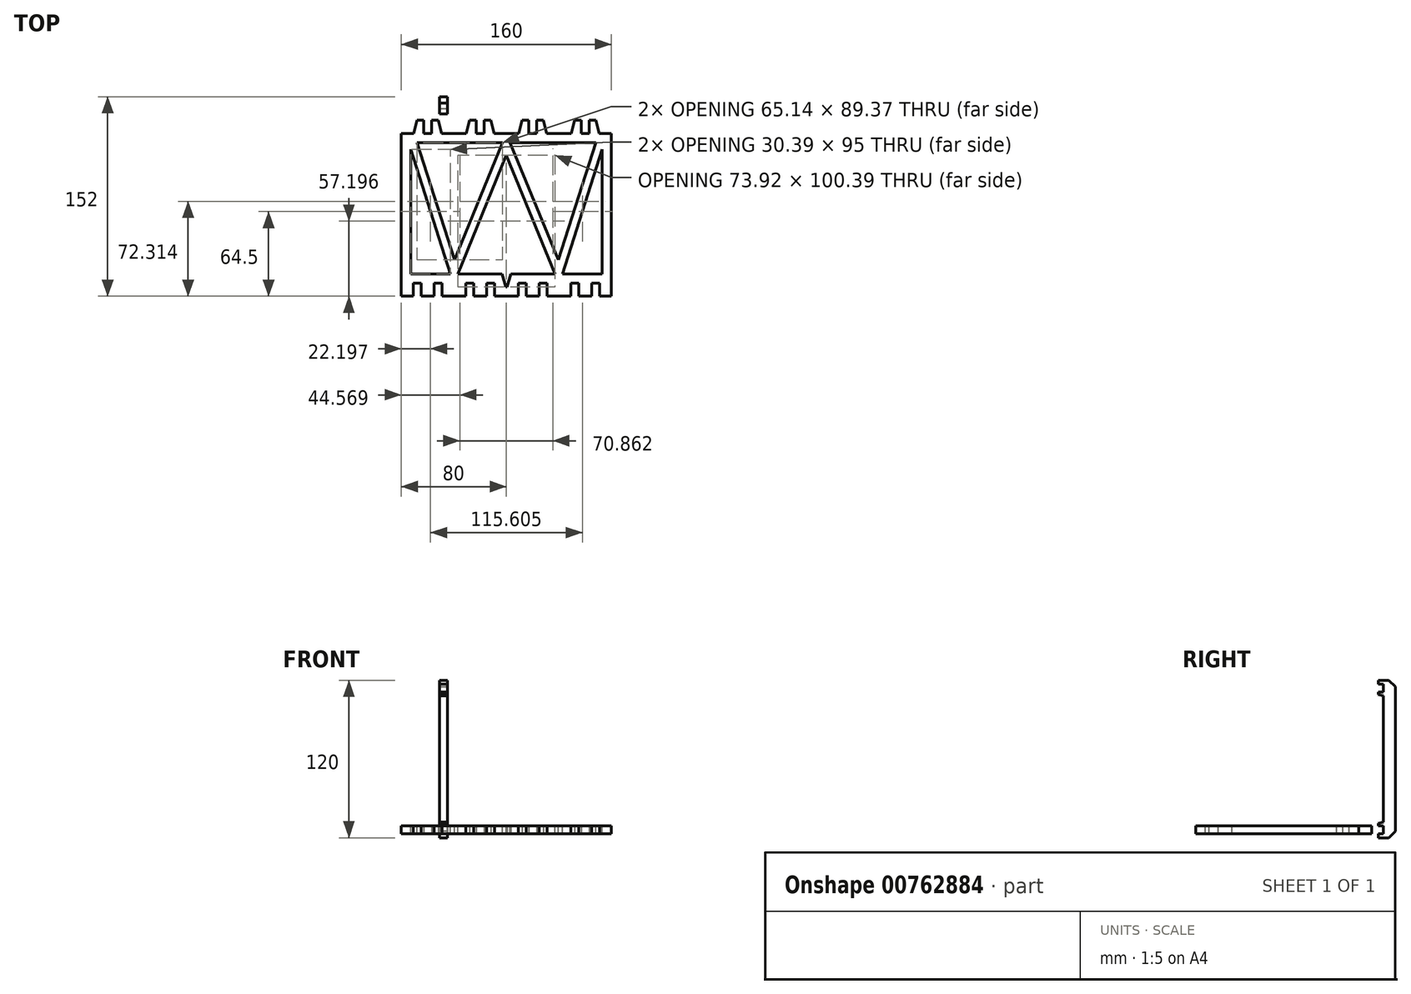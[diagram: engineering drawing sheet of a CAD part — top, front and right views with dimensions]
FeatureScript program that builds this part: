
annotation { "Feature Type Name" : "Feature", "Feature Type Description" : "" }
export const myFeature = defineFeature(function(context is Context, id is Id, definition is map)
    precondition{}
    {
        {
            assignVariable(context, id + "F0", {"name" : "bar_thick", "anyValue" : 6});
        }
        {
            var Q0;
            Q0=qCreatedBy(makeId("Top.planeOp"),FACE);
            var sketch = newSketch(context, id + "F1", { "sketchPlane" : qUnion([Q0])});
            skLineSegment(sketch, "E0", {"start": v(-20, 0) * mm, "end": v(-10.62, 0) * mm});
            skLineSegment(sketch, "E1", {"start": v(-10.62, 0) * mm, "end": v(-8, 10) * mm});
            skLineSegment(sketch, "E2", {"start": v(-8, 10) * mm, "end": v(-3, 10) * mm});
            skLineSegment(sketch, "E3", {"start": v(-3, 10) * mm, "end": v(-3, 0) * mm});
            skLineSegment(sketch, "E4", {"start": v(0, 0) * mm, "end": v(0, -7) * mm, "construction": true});
            skLineSegment(sketch, "E5", {"start": v(-3, 0) * mm, "end": v(-10.62, 0) * mm, "construction": true});
            skLineSegment(sketch, "E6", {"start": v(-20, -117) * mm, "end": v(-19.4, -117) * mm});
            skLineSegment(sketch, "E7", {"start": v(-19.4, -117) * mm, "end": v(-16.79, -107) * mm});
            skLineSegment(sketch, "E8", {"start": v(-16.79, -107) * mm, "end": v(0, -107) * mm});
            skLineSegment(sketch, "E9", {"start": v(-20, -124) * mm, "end": v(-11, -124) * mm});
            skLineSegment(sketch, "E10", {"start": v(-11, -124) * mm, "end": v(-11, -114) * mm});
            skLineSegment(sketch, "E11", {"start": v(-11, -114) * mm, "end": v(-5, -114) * mm});
            skLineSegment(sketch, "E12", {"start": v(-5, -114) * mm, "end": v(-5, -124) * mm});
            skLineSegment(sketch, "E13", {"start": v(-5, -124) * mm, "end": v(0, -124) * mm});
            skLineSegment(sketch, "E14", {"start": v(0, -117) * mm, "end": v(0, -124) * mm, "construction": true});
            skLineSegment(sketch, "E15", {"start": v(0, -7) * mm, "end": v(0, -117) * mm, "construction": true});
            skLineSegment(sketch, "E16", {"start": v(-11, -114) * mm, "end": v(-18.62, -114) * mm, "construction": true});
            skLineSegment(sketch, "E17", {"start": v(-11, -114) * mm, "end": v(-11, -107) * mm, "construction": true});
            skLineSegment(sketch, "E18", {"start": v(-19.4, -117) * mm, "end": v(-19.4, -124) * mm, "construction": true});
            skLineSegment(sketch, "E19", {"start": v(0, -7) * mm, "end": v(-20, -7) * mm});
            skLineSegment(sketch, "E20", {"start": v(-3, 0) * mm, "end": v(0, 0) * mm});
            skLineSegment(sketch, "E21", {"start": v(-20, 0) * mm, "end": v(-20, -7) * mm});
            skLineSegment(sketch, "E22", {"start": v(-20, -117) * mm, "end": v(-20, -124) * mm});
            skLineSegment(sketch, "E23", {"start": v(0, 0) * mm, "end": v(0, -7) * mm});
            skLineSegment(sketch, "E24", {"start": v(0, -107) * mm, "end": v(0, -124) * mm});
            skSolve(sketch);
        }
        {
            var Q0;
            Q0=makeQuery(id+"F1.imprint","IMPRINT",FACE,{"disambiguationData":[TD([[makeQuery(id+"F1.imprint","IMPRINT",EDGE,{"derivedFrom":sQuery(id+"F1.wireOp",EDGE,"E0")}),-1.0]])]});
            var Q1;
            Q1=makeQuery(id+"F1.imprint","IMPRINT",FACE,{"disambiguationData":[TD([[makeQuery(id+"F1.imprint","IMPRINT",EDGE,{"derivedFrom":sQuery(id+"F1.wireOp",EDGE,"E6")}),-1.0]])]});
            extrude(context, id + "F2", {"entities" : qUnion([Q0, Q1]), "depth" : (getVariable(context, 'bar_thick')) * mm, "offsetDistance" : 25 * mm});
        }
        {
            var Q0;
            Q0=makeQuery(id+"F2.opExtrude","SWEPT_BODY",BODY,{"disambiguationData":[OSD([sQuery(id+"F1.wireOp",EDGE,"E0"),sQuery(id+"F1.wireOp",EDGE,"E1"),sQuery(id+"F1.wireOp",EDGE,"E2"),sQuery(id+"F1.wireOp",EDGE,"E3"),sQuery(id+"F1.wireOp",EDGE,"E19"),sQuery(id+"F1.wireOp",EDGE,"E20"),sQuery(id+"F1.wireOp",EDGE,"E21"),sQuery(id+"F1.wireOp",EDGE,"E23")])]});
            var Q1;
            Q1=makeQuery(id+"F2.opExtrude","SWEPT_BODY",BODY,{"disambiguationData":[OSD([sQuery(id+"F1.wireOp",EDGE,"E6"),sQuery(id+"F1.wireOp",EDGE,"E7"),sQuery(id+"F1.wireOp",EDGE,"E8"),sQuery(id+"F1.wireOp",EDGE,"E9"),sQuery(id+"F1.wireOp",EDGE,"E10"),sQuery(id+"F1.wireOp",EDGE,"E11"),sQuery(id+"F1.wireOp",EDGE,"E12"),sQuery(id+"F1.wireOp",EDGE,"E13"),sQuery(id+"F1.wireOp",EDGE,"E22"),sQuery(id+"F1.wireOp",EDGE,"E24")])]});
            var Q2;
            Q2=makeQuery(id+"F2.opExtrude","SWEPT_FACE",FACE,{"disambiguationData":[OSD([sQuery(id+"F1.wireOp",EDGE,"E23")])]});
            mirror(context, id + "F3", {"operationType" : NewBodyOperationType.ADD, "entities" : qUnion([Q0, Q1]), "mirrorPlane" : qUnion([Q2])});
        }
        {
            var Q0;
            Q0=makeQuery(id+"F2.opExtrude","SWEPT_BODY",BODY,{"disambiguationData":[OSD([sQuery(id+"F1.wireOp",EDGE,"E0"),sQuery(id+"F1.wireOp",EDGE,"E1"),sQuery(id+"F1.wireOp",EDGE,"E2"),sQuery(id+"F1.wireOp",EDGE,"E3"),sQuery(id+"F1.wireOp",EDGE,"E19"),sQuery(id+"F1.wireOp",EDGE,"E20"),sQuery(id+"F1.wireOp",EDGE,"E21"),sQuery(id+"F1.wireOp",EDGE,"E23")])]});
            var Q1;
            Q1=makeQuery(id+"F2.opExtrude","SWEPT_BODY",BODY,{"disambiguationData":[OSD([sQuery(id+"F1.wireOp",EDGE,"E6"),sQuery(id+"F1.wireOp",EDGE,"E7"),sQuery(id+"F1.wireOp",EDGE,"E8"),sQuery(id+"F1.wireOp",EDGE,"E9"),sQuery(id+"F1.wireOp",EDGE,"E10"),sQuery(id+"F1.wireOp",EDGE,"E11"),sQuery(id+"F1.wireOp",EDGE,"E12"),sQuery(id+"F1.wireOp",EDGE,"E13"),sQuery(id+"F1.wireOp",EDGE,"E22"),sQuery(id+"F1.wireOp",EDGE,"E24")])]});
            var Q2;
            Q2=makeQuery(id+"F3.opPattern","COPY",FACE,{"derivedFrom":makeQuery(id+"F2.opExtrude","SWEPT_FACE",FACE,{"disambiguationData":[OSD([sQuery(id+"F1.wireOp",EDGE,"E21")])]}),"instanceName":"1"});
            mirror(context, id + "F4", {"operationType" : NewBodyOperationType.ADD, "entities" : qUnion([Q0, Q1]), "mirrorPlane" : qUnion([Q2])});
        }
        {
            var Q0;
            Q0=makeQuery(id+"F2.opExtrude","SWEPT_BODY",BODY,{"disambiguationData":[OSD([sQuery(id+"F1.wireOp",EDGE,"E0"),sQuery(id+"F1.wireOp",EDGE,"E1"),sQuery(id+"F1.wireOp",EDGE,"E2"),sQuery(id+"F1.wireOp",EDGE,"E3"),sQuery(id+"F1.wireOp",EDGE,"E19"),sQuery(id+"F1.wireOp",EDGE,"E20"),sQuery(id+"F1.wireOp",EDGE,"E21"),sQuery(id+"F1.wireOp",EDGE,"E23")])]});
            var Q1;
            Q1=makeQuery(id+"F2.opExtrude","SWEPT_BODY",BODY,{"disambiguationData":[OSD([sQuery(id+"F1.wireOp",EDGE,"E6"),sQuery(id+"F1.wireOp",EDGE,"E7"),sQuery(id+"F1.wireOp",EDGE,"E8"),sQuery(id+"F1.wireOp",EDGE,"E9"),sQuery(id+"F1.wireOp",EDGE,"E10"),sQuery(id+"F1.wireOp",EDGE,"E11"),sQuery(id+"F1.wireOp",EDGE,"E12"),sQuery(id+"F1.wireOp",EDGE,"E13"),sQuery(id+"F1.wireOp",EDGE,"E22"),sQuery(id+"F1.wireOp",EDGE,"E24")])]});
            var Q2;
            Q2=makeQuery(id+"F4.opPattern","COPY",FACE,{"derivedFrom":makeQuery(id+"F2.opExtrude","SWEPT_FACE",FACE,{"disambiguationData":[OSD([sQuery(id+"F1.wireOp",EDGE,"E21")])]}),"instanceName":"1"});
            mirror(context, id + "F5", {"operationType" : NewBodyOperationType.ADD, "entities" : qUnion([Q0, Q1]), "mirrorPlane" : qUnion([Q2])});
        }
        {
            var Q0;
            {var subQ0=makeQuery(id+"F2.opExtrude","CAP_FACE",FACE,{"disambiguationData":[OSD([sQuery(id+"F1.wireOp",EDGE,"E0"),sQuery(id+"F1.wireOp",EDGE,"E1"),sQuery(id+"F1.wireOp",EDGE,"E2"),sQuery(id+"F1.wireOp",EDGE,"E3"),sQuery(id+"F1.wireOp",EDGE,"E19"),sQuery(id+"F1.wireOp",EDGE,"E20"),sQuery(id+"F1.wireOp",EDGE,"E21"),sQuery(id+"F1.wireOp",EDGE,"E23")])],"isStart":false});var subQ1=makeQuery(id+"F3.boolean.opBoolean","MERGE",FACE,{"derivedFrom":[subQ0,makeQuery(id+"F3.opPattern","COPY",FACE,{"derivedFrom":subQ0,"instanceName":"1"})]});var subQ2=makeQuery(id+"F4.boolean.opBoolean","MERGE",FACE,{"derivedFrom":[subQ1,makeQuery(id+"F4.opPattern","COPY",FACE,{"derivedFrom":subQ1,"instanceName":"1"})]});Q0=makeQuery(id+"F5.boolean.opBoolean","MERGE",FACE,{"derivedFrom":[subQ2,makeQuery(id+"F5.opPattern","COPY",FACE,{"derivedFrom":subQ2,"instanceName":"1"})]});}
            var sketch = newSketch(context, id + "F6", { "sketchPlane" : qUnion([Q0])});
            skLineSegment(sketch, "E25", {"start": v(-20, -7) * mm, "end": v(-20, -117) * mm});
            skLineSegment(sketch, "E26", {"start": v(-20, -7) * mm, "end": v(-13, -7) * mm});
            skLineSegment(sketch, "E27", {"start": v(-13, -7) * mm, "end": v(-13, -117) * mm});
            skLineSegment(sketch, "E28", {"start": v(-13, -117) * mm, "end": v(-20, -117) * mm});
            skLineSegment(sketch, "E29", {"start": v(-20, -7) * mm, "end": v(-20, 0) * mm, "construction": true});
            skLineSegment(sketch, "E30", {"start": v(60, -7) * mm, "end": v(60, -117) * mm, "construction": true});
            skLineSegment(sketch, "E31.MirrorCS", {"start": v(140, -7) * mm, "end": v(133, -7) * mm});
            skLineSegment(sketch, "E32.MirrorCS", {"start": v(133, -117) * mm, "end": v(140, -117) * mm});
            skLineSegment(sketch, "E33.MirrorCS", {"start": v(140, -7) * mm, "end": v(140, -117) * mm});
            skLineSegment(sketch, "E34.MirrorCS", {"start": v(133, -7) * mm, "end": v(133, -117) * mm});
            skSolve(sketch);
        }
        {
            var Q0;
            Q0 = qSketchRegion(id + "F6", true);
            var Q1;
            {var subQ0=makeQuery(id+"F2.opExtrude","CAP_FACE",FACE,{"disambiguationData":[OSD([sQuery(id+"F1.wireOp",EDGE,"E0"),sQuery(id+"F1.wireOp",EDGE,"E1"),sQuery(id+"F1.wireOp",EDGE,"E2"),sQuery(id+"F1.wireOp",EDGE,"E3"),sQuery(id+"F1.wireOp",EDGE,"E19"),sQuery(id+"F1.wireOp",EDGE,"E20"),sQuery(id+"F1.wireOp",EDGE,"E21"),sQuery(id+"F1.wireOp",EDGE,"E23")])],"isStart":true});var subQ1=makeQuery(id+"F3.boolean.opBoolean","MERGE",FACE,{"derivedFrom":[subQ0,makeQuery(id+"F3.opPattern","COPY",FACE,{"derivedFrom":subQ0,"instanceName":"1"})]});var subQ2=makeQuery(id+"F4.boolean.opBoolean","MERGE",FACE,{"derivedFrom":[subQ1,makeQuery(id+"F4.opPattern","COPY",FACE,{"derivedFrom":subQ1,"instanceName":"1"})]});Q1=makeQuery(id+"F5.boolean.opBoolean","MERGE",FACE,{"derivedFrom":[subQ2,makeQuery(id+"F5.opPattern","COPY",FACE,{"derivedFrom":subQ2,"instanceName":"1"})]});}
            extrude(context, id + "F7", {"entities" : qUnion([Q0]), "operationType" : NewBodyOperationType.ADD, "endBound" : BoundingType.UP_TO_SURFACE, "oppositeDirection" : true, "depth" : 25 * mm, "endBoundEntityFace" : qUnion([Q1]), "offsetDistance" : 25 * mm});
        }
        {
            var Q0;
            {var subQ0=makeQuery(id+"F2.opExtrude","CAP_FACE",FACE,{"disambiguationData":[OSD([sQuery(id+"F1.wireOp",EDGE,"E6"),sQuery(id+"F1.wireOp",EDGE,"E7"),sQuery(id+"F1.wireOp",EDGE,"E8"),sQuery(id+"F1.wireOp",EDGE,"E9"),sQuery(id+"F1.wireOp",EDGE,"E10"),sQuery(id+"F1.wireOp",EDGE,"E11"),sQuery(id+"F1.wireOp",EDGE,"E12"),sQuery(id+"F1.wireOp",EDGE,"E13"),sQuery(id+"F1.wireOp",EDGE,"E22"),sQuery(id+"F1.wireOp",EDGE,"E24")])],"isStart":false});var subQ1=makeQuery(id+"F3.boolean.opBoolean","MERGE",FACE,{"derivedFrom":[subQ0,makeQuery(id+"F3.opPattern","COPY",FACE,{"derivedFrom":subQ0,"instanceName":"1"})]});var subQ2=makeQuery(id+"F4.boolean.opBoolean","MERGE",FACE,{"derivedFrom":[subQ1,makeQuery(id+"F4.opPattern","COPY",FACE,{"derivedFrom":subQ1,"instanceName":"1"})]});var subQ3=makeQuery(id+"F2.opExtrude","CAP_FACE",FACE,{"disambiguationData":[OSD([sQuery(id+"F1.wireOp",EDGE,"E0"),sQuery(id+"F1.wireOp",EDGE,"E1"),sQuery(id+"F1.wireOp",EDGE,"E2"),sQuery(id+"F1.wireOp",EDGE,"E3"),sQuery(id+"F1.wireOp",EDGE,"E19"),sQuery(id+"F1.wireOp",EDGE,"E20"),sQuery(id+"F1.wireOp",EDGE,"E21"),sQuery(id+"F1.wireOp",EDGE,"E23")])],"isStart":false});var subQ4=makeQuery(id+"F3.boolean.opBoolean","MERGE",FACE,{"derivedFrom":[subQ3,makeQuery(id+"F3.opPattern","COPY",FACE,{"derivedFrom":subQ3,"instanceName":"1"})]});var subQ5=makeQuery(id+"F4.boolean.opBoolean","MERGE",FACE,{"derivedFrom":[subQ4,makeQuery(id+"F4.opPattern","COPY",FACE,{"derivedFrom":subQ4,"instanceName":"1"})]});Q0=makeQuery(id+"F7.boolean.opBoolean","MERGE",FACE,{"derivedFrom":[makeQuery(id+"F5.boolean.opBoolean","MERGE",FACE,{"derivedFrom":[subQ5,makeQuery(id+"F5.opPattern","COPY",FACE,{"derivedFrom":subQ5,"instanceName":"1"})]}),makeQuery(id+"F5.boolean.opBoolean","MERGE",FACE,{"derivedFrom":[subQ2,makeQuery(id+"F5.opPattern","COPY",FACE,{"derivedFrom":subQ2,"instanceName":"1"})]}),makeQuery(id+"F7.opExtrude","CAP_FACE",FACE,{"disambiguationData":[OSD([sQuery(id+"F6.wireOp",EDGE,"E25"),sQuery(id+"F6.wireOp",EDGE,"E26"),sQuery(id+"F6.wireOp",EDGE,"E27"),sQuery(id+"F6.wireOp",EDGE,"E28")])],"isStart":true}),makeQuery(id+"F7.opExtrude","CAP_FACE",FACE,{"disambiguationData":[OSD([sQuery(id+"F6.wireOp",EDGE,"E31.MirrorCS"),sQuery(id+"F6.wireOp",EDGE,"E32.MirrorCS"),sQuery(id+"F6.wireOp",EDGE,"E33.MirrorCS"),sQuery(id+"F6.wireOp",EDGE,"E34.MirrorCS")])],"isStart":true})]});}
            var sketch = newSketch(context, id + "F8", { "sketchPlane" : qUnion([Q0])});
            skLineSegment(sketch, "E35", {"start": v(-13, -7) * mm, "end": v(-8, -7) * mm});
            skLineSegment(sketch, "E36", {"start": v(-8, -7) * mm, "end": v(20.6, -96.37) * mm});
            skLineSegment(sketch, "E37", {"start": v(20.6, -96.37) * mm, "end": v(60, 0) * mm});
            skLineSegment(sketch, "E38", {"start": v(60, 0) * mm, "end": v(60, -16.6) * mm});
            skLineSegment(sketch, "E39", {"start": v(60, -16.6) * mm, "end": v(23.04, -107) * mm});
            skLineSegment(sketch, "E40", {"start": v(-13, -7) * mm, "end": v(-13, -12) * mm});
            skLineSegment(sketch, "E41", {"start": v(20.6, -117) * mm, "end": v(23.21, -107) * mm});
            skLineSegment(sketch, "E42", {"start": v(23.04, -107) * mm, "end": v(23.21, -107) * mm});
            skLineSegment(sketch, "E43", {"start": v(20.6, -117) * mm, "end": v(-13, -12) * mm});
            skLineSegment(sketch, "E44", {"start": v(40.3, -48.19) * mm, "end": v(46.12, -50.57) * mm, "construction": true});
            skLineSegment(sketch, "E45", {"start": v(6.3, -51.69) * mm, "end": v(0.31, -53.6) * mm, "construction": true});
            skLineSegment(sketch, "E46.MirrorCS", {"start": v(99.4, -96.37) * mm, "end": v(60, 0) * mm});
            skLineSegment(sketch, "E47.MirrorCS", {"start": v(60, -16.6) * mm, "end": v(96.96, -107) * mm});
            skLineSegment(sketch, "E48.MirrorCS", {"start": v(96.96, -107) * mm, "end": v(96.79, -107) * mm});
            skLineSegment(sketch, "E49.MirrorCS", {"start": v(99.4, -117) * mm, "end": v(96.79, -107) * mm});
            skLineSegment(sketch, "E50.MirrorCS", {"start": v(99.4, -117) * mm, "end": v(133, -12) * mm});
            skLineSegment(sketch, "E51.MirrorCS", {"start": v(128, -7) * mm, "end": v(99.4, -96.37) * mm});
            skLineSegment(sketch, "E52.MirrorCS", {"start": v(133, -7) * mm, "end": v(128, -7) * mm});
            skLineSegment(sketch, "E53.MirrorCS", {"start": v(133, -7) * mm, "end": v(133, -12) * mm});
            skLineSegment(sketch, "E54", {"start": v(16.79, -107) * mm, "end": v(17.4, -107) * mm});
            skLineSegment(sketch, "E55", {"start": v(16.79, -107) * mm, "end": v(19.4, -117) * mm});
            skLineSegment(sketch, "E56", {"start": v(19.4, -117) * mm, "end": v(20.6, -117) * mm});
            skLineSegment(sketch, "E57.MirrorCS", {"start": v(100.6, -117) * mm, "end": v(99.4, -117) * mm});
            skLineSegment(sketch, "E58.MirrorCS", {"start": v(103.21, -107) * mm, "end": v(100.6, -117) * mm});
            skLineSegment(sketch, "E59.MirrorCS", {"start": v(103.21, -107) * mm, "end": v(102.6, -107) * mm});
            skSolve(sketch);
        }
        {
            var Q0;
            Q0=makeQuery(id+"F8.imprint","IMPRINT",FACE,{"disambiguationData":[TD([[makeQuery(id+"F8.imprint","IMPRINT",EDGE,{"derivedFrom":sQuery(id+"F8.wireOp",EDGE,"E35")}),1.0]])]});
            var Q1;
            {var subQ0=sQuery(id+"F8.wireOp",EDGE,"E47.MirrorCS");Q1=makeQuery(id+"F8.imprint","IMPRINT",FACE,{"disambiguationData":[TD([[makeQuery(id+"F8.imprint","IMPRINT",EDGE,{"derivedFrom":subQ0}),1.0]])]});}
            var Q2;
            {var subQ2=sQuery(id+"F8.wireOp",EDGE,"E54");Q2=makeQuery(id+"F8.imprint","IMPRINT",FACE,{"disambiguationData":[TD([[makeQuery(id+"F8.imprint","IMPRINT",EDGE,{"derivedFrom":subQ2}),-1.0]])]});}
            var Q3;
            {var subQ0=sQuery(id+"F8.wireOp",EDGE,"E57.MirrorCS");Q3=makeQuery(id+"F8.imprint","IMPRINT",FACE,{"disambiguationData":[TD([[makeQuery(id+"F8.imprint","IMPRINT",EDGE,{"derivedFrom":subQ0}),1.0]])]});}
            var Q4;
            Q4=makeQuery(id+"F7.opExtrude","CAP_VERTEX",VERTEX,{"disambiguationData":[OSD([sQuery(id+"F1.wireOp",EDGE,"E0"),sQuery(id+"F1.wireOp",EDGE,"E1"),sQuery(id+"F1.wireOp",EDGE,"E2"),sQuery(id+"F1.wireOp",EDGE,"E3"),sQuery(id+"F1.wireOp",EDGE,"E19"),sQuery(id+"F1.wireOp",EDGE,"E20"),sQuery(id+"F1.wireOp",EDGE,"E21"),sQuery(id+"F1.wireOp",EDGE,"E23"),sQuery(id+"F6.wireOp",EDGE,"E31.MirrorCS"),sQuery(id+"F6.wireOp",EDGE,"E34.MirrorCS")])],"isStart":false});
            extrude(context, id + "F9", {"entities" : qUnion([Q0, Q1, Q2, Q3]), "operationType" : NewBodyOperationType.ADD, "endBound" : BoundingType.UP_TO_VERTEX, "oppositeDirection" : true, "depth" : 25 * mm, "endBoundEntityVertex" : qUnion([Q4]), "offsetDistance" : 25 * mm});
        }
        {
            var Q0;
            Q0=qCreatedBy(makeId("Top.planeOp"),FACE);
            var sketch = newSketch(context, id + "F10", { "sketchPlane" : qUnion([Q0])});
            skLineSegment(sketch, "E60", {"start": v(0, 28) * mm, "end": v(0, 15) * mm});
            skLineSegment(sketch, "E61", {"start": v(0, 15) * mm, "end": v(3, 15) * mm});
            skLineSegment(sketch, "E62", {"start": v(3, 15) * mm, "end": v(3, 19) * mm});
            skLineSegment(sketch, "E63", {"start": v(3, 19) * mm, "end": v(9, 19) * mm});
            skLineSegment(sketch, "E64", {"start": v(9, 19) * mm, "end": v(9, 15) * mm});
            skLineSegment(sketch, "E65", {"start": v(0, 28) * mm, "end": v(60, 28) * mm});
            skLineSegment(sketch, "E66", {"start": v(60, 28) * mm, "end": v(60, 19) * mm, "construction": true});
            skLineSegment(sketch, "E67", {"start": v(9, 19) * mm, "end": v(9, 28) * mm, "construction": true});
            skLineSegment(sketch, "E68", {"start": v(9, 15) * mm, "end": v(11, 15) * mm});
            skLineSegment(sketch, "E69", {"start": v(11, 15) * mm, "end": v(12, 19) * mm});
            skLineSegment(sketch, "E70", {"start": v(12, 19) * mm, "end": v(60, 19) * mm});
            skLineSegment(sketch, "E71", {"start": v(9, 19) * mm, "end": v(12, 19) * mm, "construction": true});
            skLineSegment(sketch, "E72.MirrorCS", {"start": v(120, 15) * mm, "end": v(117, 15) * mm});
            skLineSegment(sketch, "E73.MirrorCS", {"start": v(111, 15) * mm, "end": v(109, 15) * mm});
            skLineSegment(sketch, "E74.MirrorCS", {"start": v(109, 15) * mm, "end": v(108, 19) * mm});
            skLineSegment(sketch, "E75.MirrorCS", {"start": v(111, 19) * mm, "end": v(111, 15) * mm});
            skLineSegment(sketch, "E76.MirrorCS", {"start": v(117, 15) * mm, "end": v(117, 19) * mm});
            skLineSegment(sketch, "E77.MirrorCS", {"start": v(120, 28) * mm, "end": v(60, 28) * mm});
            skLineSegment(sketch, "E78.MirrorCS", {"start": v(117, 19) * mm, "end": v(111, 19) * mm});
            skLineSegment(sketch, "E79.MirrorCS", {"start": v(120, 28) * mm, "end": v(120, 15) * mm});
            skLineSegment(sketch, "E80.MirrorCS", {"start": v(108, 19) * mm, "end": v(60, 19) * mm});
            skLineSegment(sketch, "E81", {"start": v(0, 0) * mm, "end": v(0, 15) * mm, "construction": true});
            skSolve(sketch);
        }
        {
            var Q0;
            Q0=makeQuery(id+"F10.imprint","IMPRINT",FACE,{"disambiguationData":[TD([[makeQuery(id+"F10.imprint","IMPRINT",EDGE,{"derivedFrom":sQuery(id+"F10.wireOp",EDGE,"E60")}),1.0]])]});
            extrude(context, id + "F11", {"entities" : qUnion([Q0]), "depth" : (getVariable(context, 'bar_thick')) * mm, "offsetDistance" : 25 * mm});
        }
        {
            var Q0;
            Q0=makeQuery(id+"F9.opExtrude","SWEPT_EDGE",EDGE,{"disambiguationData":[OSD([sQuery(id+"F8.wireOp",EDGE,"E43"),sQuery(id+"F8.wireOp",EDGE,"E54")])]});
            var Q1;
            Q1=makeQuery(id+"F9.opExtrude","SWEPT_EDGE",EDGE,{"disambiguationData":[OSD([sQuery(id+"F8.wireOp",EDGE,"E39"),sQuery(id+"F8.wireOp",EDGE,"E42")])]});
            var Q2;
            {var subQ0=makeQuery(id+"F2.opExtrude","SWEPT_FACE",FACE,{"disambiguationData":[OSD([sQuery(id+"F1.wireOp",EDGE,"E8")])]});Q2=makeQuery(id+"F7.boolean.opBoolean","INTERSECT",EDGE,{"derivedFrom":[makeQuery(id+"F3.boolean.opBoolean","MERGE",FACE,{"derivedFrom":[subQ0,makeQuery(id+"F3.opPattern","COPY",FACE,{"derivedFrom":subQ0,"instanceName":"1"})]}),makeQuery(id+"F7.opExtrude","SWEPT_FACE",FACE,{"disambiguationData":[OSD([sQuery(id+"F6.wireOp",EDGE,"E27")])]})]});}
            var Q3;
            Q3=makeQuery(id+"F4.opPattern","COPY",EDGE,{"derivedFrom":makeQuery(id+"F2.opExtrude","SWEPT_EDGE",EDGE,{"disambiguationData":[OSD([sQuery(id+"F1.wireOp",EDGE,"E6"),sQuery(id+"F1.wireOp",EDGE,"E7")])]}),"instanceName":"1"});
            var Q4;
            Q4=makeQuery(id+"F5.opPattern","COPY",EDGE,{"derivedFrom":makeQuery(id+"F4.opPattern","COPY",EDGE,{"derivedFrom":makeQuery(id+"F2.opExtrude","SWEPT_EDGE",EDGE,{"disambiguationData":[OSD([sQuery(id+"F1.wireOp",EDGE,"E6"),sQuery(id+"F1.wireOp",EDGE,"E7")])]}),"instanceName":"1"}),"instanceName":"1"});
            var Q5;
            Q5=makeQuery(id+"F9.opExtrude","SWEPT_EDGE",EDGE,{"disambiguationData":[OSD([sQuery(id+"F8.wireOp",EDGE,"E50.MirrorCS"),sQuery(id+"F8.wireOp",EDGE,"E59.MirrorCS")])]});
            var Q6;
            Q6=makeQuery(id+"F9.opExtrude","SWEPT_EDGE",EDGE,{"disambiguationData":[OSD([sQuery(id+"F8.wireOp",EDGE,"E47.MirrorCS"),sQuery(id+"F8.wireOp",EDGE,"E48.MirrorCS")])]});
            var Q7;
            {var subQ0=makeQuery(id+"F2.opExtrude","SWEPT_FACE",FACE,{"disambiguationData":[OSD([sQuery(id+"F1.wireOp",EDGE,"E8")])]});Q7=makeQuery(id+"F7.boolean.opBoolean","INTERSECT",EDGE,{"derivedFrom":[makeQuery(id+"F5.opPattern","COPY",FACE,{"derivedFrom":makeQuery(id+"F3.boolean.opBoolean","MERGE",FACE,{"derivedFrom":[subQ0,makeQuery(id+"F3.opPattern","COPY",FACE,{"derivedFrom":subQ0,"instanceName":"1"})]}),"instanceName":"1"}),makeQuery(id+"F7.opExtrude","SWEPT_FACE",FACE,{"disambiguationData":[OSD([sQuery(id+"F6.wireOp",EDGE,"E34.MirrorCS")])]})]});}
            var Q8;
            Q8=makeQuery(id+"F9.opExtrude","SWEPT_EDGE",EDGE,{"disambiguationData":[OSD([sQuery(id+"F1.wireOp",EDGE,"E19"),sQuery(id+"F8.wireOp",EDGE,"E51.MirrorCS"),sQuery(id+"F8.wireOp",EDGE,"E52.MirrorCS")])]});
            var Q9;
            Q9=makeQuery(id+"F9.opExtrude","SWEPT_EDGE",EDGE,{"disambiguationData":[OSD([sQuery(id+"F1.wireOp",EDGE,"E19"),sQuery(id+"F8.wireOp",EDGE,"E37")])]});
            var Q10;
            Q10=makeQuery(id+"F9.opExtrude","SWEPT_EDGE",EDGE,{"disambiguationData":[OSD([sQuery(id+"F1.wireOp",EDGE,"E19"),sQuery(id+"F8.wireOp",EDGE,"E46.MirrorCS")])]});
            var Q11;
            Q11=makeQuery(id+"F9.opExtrude","SWEPT_EDGE",EDGE,{"disambiguationData":[OSD([sQuery(id+"F1.wireOp",EDGE,"E19"),sQuery(id+"F8.wireOp",EDGE,"E35"),sQuery(id+"F8.wireOp",EDGE,"E36")])]});
            var Q12;
            Q12=makeQuery(id+"F5.opPattern","COPY",EDGE,{"derivedFrom":makeQuery(id+"F2.opExtrude","SWEPT_EDGE",EDGE,{"disambiguationData":[OSD([sQuery(id+"F1.wireOp",EDGE,"E0"),sQuery(id+"F1.wireOp",EDGE,"E21")])]}),"instanceName":"1"});
            var Q13;
            Q13=makeQuery(id+"F2.opExtrude","SWEPT_EDGE",EDGE,{"disambiguationData":[OSD([sQuery(id+"F1.wireOp",EDGE,"E0"),sQuery(id+"F1.wireOp",EDGE,"E21")])]});
            var Q14;
            Q14=makeQuery(id+"F2.opExtrude","SWEPT_EDGE",EDGE,{"disambiguationData":[OSD([sQuery(id+"F1.wireOp",EDGE,"E9"),sQuery(id+"F1.wireOp",EDGE,"E22")])]});
            var Q15;
            Q15=makeQuery(id+"F5.opPattern","COPY",EDGE,{"derivedFrom":makeQuery(id+"F2.opExtrude","SWEPT_EDGE",EDGE,{"disambiguationData":[OSD([sQuery(id+"F1.wireOp",EDGE,"E9"),sQuery(id+"F1.wireOp",EDGE,"E22")])]}),"instanceName":"1"});
            var Q16;
            Q16=makeQuery(id+"F11.opExtrude","SWEPT_EDGE",EDGE,{"disambiguationData":[OSD([sQuery(id+"F10.wireOp",EDGE,"E77.MirrorCS"),sQuery(id+"F10.wireOp",EDGE,"E79.MirrorCS")])]});
            var Q17;
            Q17=makeQuery(id+"F11.opExtrude","SWEPT_EDGE",EDGE,{"disambiguationData":[OSD([sQuery(id+"F10.wireOp",EDGE,"E60"),sQuery(id+"F10.wireOp",EDGE,"E65")])]});
            chamfer(context, id + "F12", {"entities" : qUnion([Q0, Q1, Q2, Q3, Q4, Q5, Q6, Q7, Q8, Q9, Q10, Q11, Q12, Q13, Q14, Q15, Q16, Q17]), "width" : 5 * mm, "tangentPropagation" : true});
        }
        {
            var Q0;
            Q0=makeQuery(id+"F11.opExtrude","SWEPT_BODY",BODY,{"disambiguationData":[OSD([sQuery(id+"F10.wireOp",EDGE,"E60"),sQuery(id+"F10.wireOp",EDGE,"E61"),sQuery(id+"F10.wireOp",EDGE,"E62"),sQuery(id+"F10.wireOp",EDGE,"E63"),sQuery(id+"F10.wireOp",EDGE,"E64"),sQuery(id+"F10.wireOp",EDGE,"E65"),sQuery(id+"F10.wireOp",EDGE,"E68"),sQuery(id+"F10.wireOp",EDGE,"E69"),sQuery(id+"F10.wireOp",EDGE,"E70"),sQuery(id+"F10.wireOp",EDGE,"E72.MirrorCS"),sQuery(id+"F10.wireOp",EDGE,"E73.MirrorCS"),sQuery(id+"F10.wireOp",EDGE,"E74.MirrorCS"),sQuery(id+"F10.wireOp",EDGE,"E75.MirrorCS"),sQuery(id+"F10.wireOp",EDGE,"E76.MirrorCS"),sQuery(id+"F10.wireOp",EDGE,"E77.MirrorCS"),sQuery(id+"F10.wireOp",EDGE,"E78.MirrorCS"),sQuery(id+"F10.wireOp",EDGE,"E79.MirrorCS"),sQuery(id+"F10.wireOp",EDGE,"E80.MirrorCS")])]});
            var Q1;
            Q1=makeQuery(id+"F11.opExtrude","CAP_EDGE",EDGE,{"disambiguationData":[OSD([sQuery(id+"F10.wireOp",EDGE,"E60")])],"isStart":false});
            var Q2;
            Q2=makeQuery(id+"F11.opExtrude","CAP_EDGE",EDGE,{"disambiguationData":[OSD([sQuery(id+"F10.wireOp",EDGE,"E64")])],"isStart":false});
            transform(context, id + "F13", {"entities" : qUnion([Q0]), "transformType" : TransformType.ROTATION, "transformAxis" : qUnion([Q2]), "angle" : 90 * degree, "makeCopy" : false});
        }
    });
